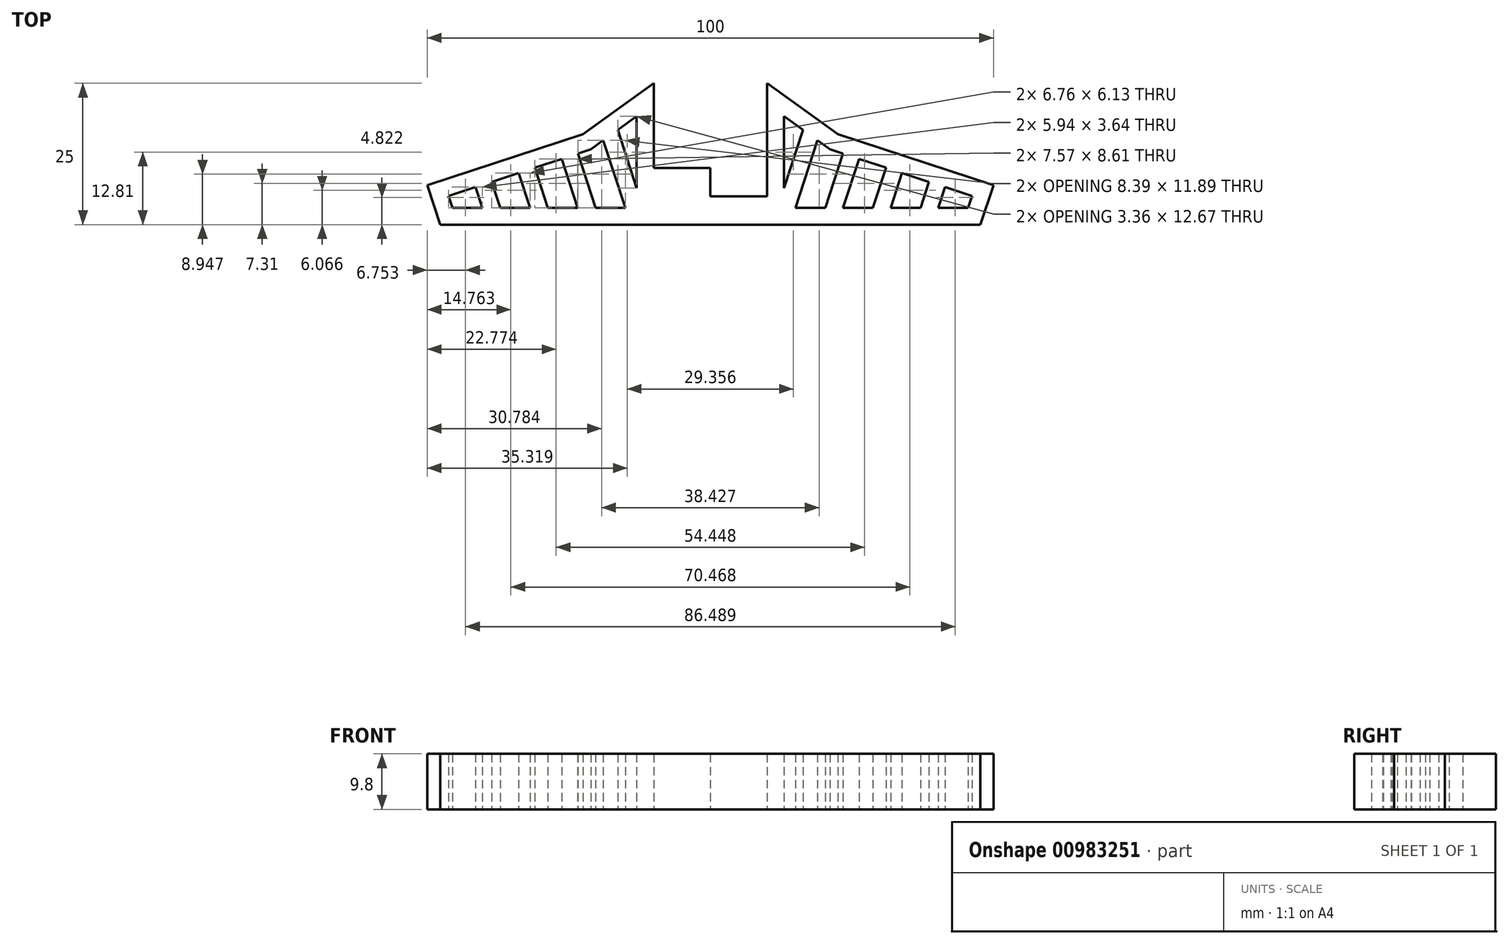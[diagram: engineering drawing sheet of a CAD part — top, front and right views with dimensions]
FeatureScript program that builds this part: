
annotation { "Feature Type Name" : "Feature", "Feature Type Description" : "" }
export const myFeature = defineFeature(function(context is Context, id is Id, definition is map)
    precondition{}
    {
        {
            var Q0;
            Q0=qCreatedBy(makeId("Top.planeOp"),FACE);
            var sketch = newSketch(context, id + "F0", { "sketchPlane" : qUnion([Q0])});
            skLineSegment(sketch, "E0", {"start": v(-58.08, -34.87) * mm, "end": v(41.92, -34.87) * mm});
            skLineSegment(sketch, "E1", {"start": v(-58.08, -34.87) * mm, "end": v(-58.08, -27.87) * mm});
            skLineSegment(sketch, "E2", {"start": v(-58.08, -27.87) * mm, "end": v(-30.58, -18.87) * mm});
            skLineSegment(sketch, "E3", {"start": v(-30.58, -18.87) * mm, "end": v(-18.08, -9.87) * mm});
            skLineSegment(sketch, "E4", {"start": v(-18.08, -9.87) * mm, "end": v(-18.08, -34.87) * mm});
            skLineSegment(sketch, "E5", {"start": v(41.92, -34.87) * mm, "end": v(41.92, -27.87) * mm});
            skLineSegment(sketch, "E6", {"start": v(41.92, -27.87) * mm, "end": v(14.42, -18.87) * mm});
            skLineSegment(sketch, "E7", {"start": v(14.42, -18.87) * mm, "end": v(1.92, -9.87) * mm});
            skLineSegment(sketch, "E8", {"start": v(1.92, -9.87) * mm, "end": v(1.92, -34.87) * mm});
            skLineSegment(sketch, "E9", {"start": v(-58.08, -27.87) * mm, "end": v(-55.8, -34.87) * mm});
            skLineSegment(sketch, "E10", {"start": v(41.92, -27.87) * mm, "end": v(39.63, -34.87) * mm});
            skLineSegment(sketch, "E11", {"start": v(1.92, -29.87) * mm, "end": v(-18.08, -29.87) * mm});
            skLineSegment(sketch, "E12", {"start": v(1.92, -24.87) * mm, "end": v(-18.08, -24.87) * mm});
            skLineSegment(sketch, "E13", {"start": v(-8.08, -34.87) * mm, "end": v(-8.08, -24.87) * mm});
            skLineSegment(sketch, "E14", {"start": v(-55.8, -34.87) * mm, "end": v(-18.08, -34.87) * mm});
            skLineSegment(sketch, "E15", {"start": v(1.92, -34.87) * mm, "end": v(39.63, -34.87) * mm});
            skLineSegment(sketch, "E16.0", {"start": v(4.92, -31.87) * mm, "end": v(37.45, -31.87) * mm});
            skLineSegment(sketch, "E16.1", {"start": v(38.13, -29.78) * mm, "end": v(37.45, -31.87) * mm});
            skLineSegment(sketch, "E16.2", {"start": v(4.92, -15.72) * mm, "end": v(4.92, -31.87) * mm});
            skLineSegment(sketch, "E16.3", {"start": v(13.04, -21.57) * mm, "end": v(4.92, -15.72) * mm});
            skLineSegment(sketch, "E16.4", {"start": v(38.13, -29.78) * mm, "end": v(13.04, -21.57) * mm});
            skLineSegment(sketch, "E17.0", {"start": v(-21.08, -15.72) * mm, "end": v(-21.08, -31.87) * mm});
            skLineSegment(sketch, "E17.1", {"start": v(-53.62, -31.87) * mm, "end": v(-21.08, -31.87) * mm});
            skLineSegment(sketch, "E17.2", {"start": v(-29.2, -21.57) * mm, "end": v(-21.08, -15.72) * mm});
            skLineSegment(sketch, "E17.3", {"start": v(-54.3, -29.78) * mm, "end": v(-29.2, -21.57) * mm});
            skLineSegment(sketch, "E17.4", {"start": v(-54.3, -29.78) * mm, "end": v(-53.62, -31.87) * mm});
            skLineSegment(sketch, "E18", {"start": v(-49.55, -28.23) * mm, "end": v(-48.36, -31.87) * mm});
            skLineSegment(sketch, "E19", {"start": v(-46.7, -27.3) * mm, "end": v(-45.2, -31.87) * mm});
            skLineSegment(sketch, "E20", {"start": v(-41.94, -25.74) * mm, "end": v(-39.94, -31.87) * mm});
            skLineSegment(sketch, "E21", {"start": v(-39.1, -24.8) * mm, "end": v(-36.78, -31.87) * mm});
            skLineSegment(sketch, "E22", {"start": v(-34.34, -23.25) * mm, "end": v(-31.52, -31.87) * mm});
            skLineSegment(sketch, "E23", {"start": v(-31.49, -22.32) * mm, "end": v(-28.36, -31.87) * mm});
            skLineSegment(sketch, "E24", {"start": v(-27, -19.98) * mm, "end": v(-23.1, -31.87) * mm});
            skLineSegment(sketch, "E25", {"start": v(-24.44, -18.14) * mm, "end": v(-21.08, -28.4) * mm});
            skLineSegment(sketch, "E26", {"start": v(33.38, -28.23) * mm, "end": v(32.2, -31.87) * mm});
            skLineSegment(sketch, "E27", {"start": v(30.53, -27.3) * mm, "end": v(29.03, -31.87) * mm});
            skLineSegment(sketch, "E28", {"start": v(25.78, -25.74) * mm, "end": v(23.77, -31.87) * mm});
            skLineSegment(sketch, "E29", {"start": v(22.93, -24.8) * mm, "end": v(20.62, -31.87) * mm});
            skLineSegment(sketch, "E30", {"start": v(18.17, -23.25) * mm, "end": v(15.36, -31.87) * mm});
            skLineSegment(sketch, "E31", {"start": v(15.32, -22.32) * mm, "end": v(12.2, -31.87) * mm});
            skLineSegment(sketch, "E32", {"start": v(10.83, -19.98) * mm, "end": v(6.94, -31.87) * mm});
            skLineSegment(sketch, "E33", {"start": v(8.27, -18.14) * mm, "end": v(4.92, -28.4) * mm});
            skSolve(sketch);
        }
        {
            var Q0;
            {var subQ0=sQuery(id+"F0.wireOp",EDGE,"E18");Q0=makeQuery(id+"F0.imprint","IMPRINT",FACE,{"disambiguationData":[TD([[makeQuery(id+"F0.imprint","IMPRINT",EDGE,{"derivedFrom":subQ0}),1.0]])]});}
            var Q1;
            {var subQ2=sQuery(id+"F0.wireOp",EDGE,"E20");Q1=makeQuery(id+"F0.imprint","IMPRINT",FACE,{"disambiguationData":[TD([[makeQuery(id+"F0.imprint","IMPRINT",EDGE,{"derivedFrom":subQ2}),1.0]])]});}
            var Q2;
            {var subQ0=sQuery(id+"F0.wireOp",EDGE,"E22");Q2=makeQuery(id+"F0.imprint","IMPRINT",FACE,{"disambiguationData":[TD([[makeQuery(id+"F0.imprint","IMPRINT",EDGE,{"derivedFrom":subQ0}),1.0]])]});}
            var Q3;
            {var subQ0=sQuery(id+"F0.wireOp",EDGE,"E24");Q3=makeQuery(id+"F0.imprint","IMPRINT",FACE,{"disambiguationData":[TD([[makeQuery(id+"F0.imprint","IMPRINT",EDGE,{"derivedFrom":subQ0}),1.0]])]});}
            var Q4;
            {var subQ0=sQuery(id+"F0.wireOp",EDGE,"E4");var subQ1=sQuery(id+"F0.wireOp",EDGE,"E0");var subQ2=makeQuery(id+"F0.imprint","INTERSECT",VERTEX,{"derivedFrom":[subQ1,subQ0]});Q4=makeQuery(id+"F0.imprint","IMPRINT",FACE,{"disambiguationData":[TD([[makeQuery(id+"F0.imprint","IMPRINT",EDGE,{"disambiguationData":[TD([[subQ2,-1.0]])],"derivedFrom":subQ1}),1.0]])]});}
            var Q5;
            {var subQ0=sQuery(id+"F0.wireOp",EDGE,"E8");var subQ1=sQuery(id+"F0.wireOp",EDGE,"E0");var subQ2=makeQuery(id+"F0.imprint","INTERSECT",VERTEX,{"derivedFrom":[subQ1,subQ0]});Q5=makeQuery(id+"F0.imprint","IMPRINT",FACE,{"disambiguationData":[TD([[makeQuery(id+"F0.imprint","IMPRINT",EDGE,{"disambiguationData":[TD([[subQ2,1.0]])],"derivedFrom":subQ1}),1.0]])]});}
            var Q6;
            {var subQ0=sQuery(id+"F0.wireOp",EDGE,"E11");var subQ1=sQuery(id+"F0.wireOp",EDGE,"E4");var subQ2=makeQuery(id+"F0.imprint","INTERSECT",VERTEX,{"derivedFrom":[subQ1,subQ0]});Q6=makeQuery(id+"F0.imprint","IMPRINT",FACE,{"disambiguationData":[TD([[makeQuery(id+"F0.imprint","IMPRINT",EDGE,{"disambiguationData":[TD([[subQ2,1.0]])],"derivedFrom":subQ1}),1.0]])]});}
            var Q7;
            Q7=makeQuery(id+"F0.imprint","IMPRINT",FACE,{"disambiguationData":[TD([[makeQuery(id+"F0.imprint","IMPRINT",EDGE,{"derivedFrom":sQuery(id+"F0.wireOp",EDGE,"E2")}),-1.0]])]});
            var Q8;
            Q8=makeQuery(id+"F0.imprint","IMPRINT",FACE,{"disambiguationData":[TD([[makeQuery(id+"F0.imprint","IMPRINT",EDGE,{"derivedFrom":sQuery(id+"F0.wireOp",EDGE,"E6")}),1.0]])]});
            var Q9;
            {var subQ0=sQuery(id+"F0.wireOp",EDGE,"E32");Q9=makeQuery(id+"F0.imprint","IMPRINT",FACE,{"disambiguationData":[TD([[makeQuery(id+"F0.imprint","IMPRINT",EDGE,{"derivedFrom":subQ0}),-1.0]])]});}
            var Q10;
            {var subQ0=sQuery(id+"F0.wireOp",EDGE,"E30");Q10=makeQuery(id+"F0.imprint","IMPRINT",FACE,{"disambiguationData":[TD([[makeQuery(id+"F0.imprint","IMPRINT",EDGE,{"derivedFrom":subQ0}),-1.0]])]});}
            var Q11;
            {var subQ0=sQuery(id+"F0.wireOp",EDGE,"E28");Q11=makeQuery(id+"F0.imprint","IMPRINT",FACE,{"disambiguationData":[TD([[makeQuery(id+"F0.imprint","IMPRINT",EDGE,{"derivedFrom":subQ0}),-1.0]])]});}
            var Q12;
            {var subQ0=sQuery(id+"F0.wireOp",EDGE,"E26");Q12=makeQuery(id+"F0.imprint","IMPRINT",FACE,{"disambiguationData":[TD([[makeQuery(id+"F0.imprint","IMPRINT",EDGE,{"derivedFrom":subQ0}),-1.0]])]});}
            extrude(context, id + "F1", {"entities" : qUnion([Q0, Q1, Q2, Q3, Q4, Q5, Q6, Q7, Q8, Q9, Q10, Q11, Q12]), "depth" : 9.8 * mm, "offsetDistance" : 25 * mm});
        }
    });
